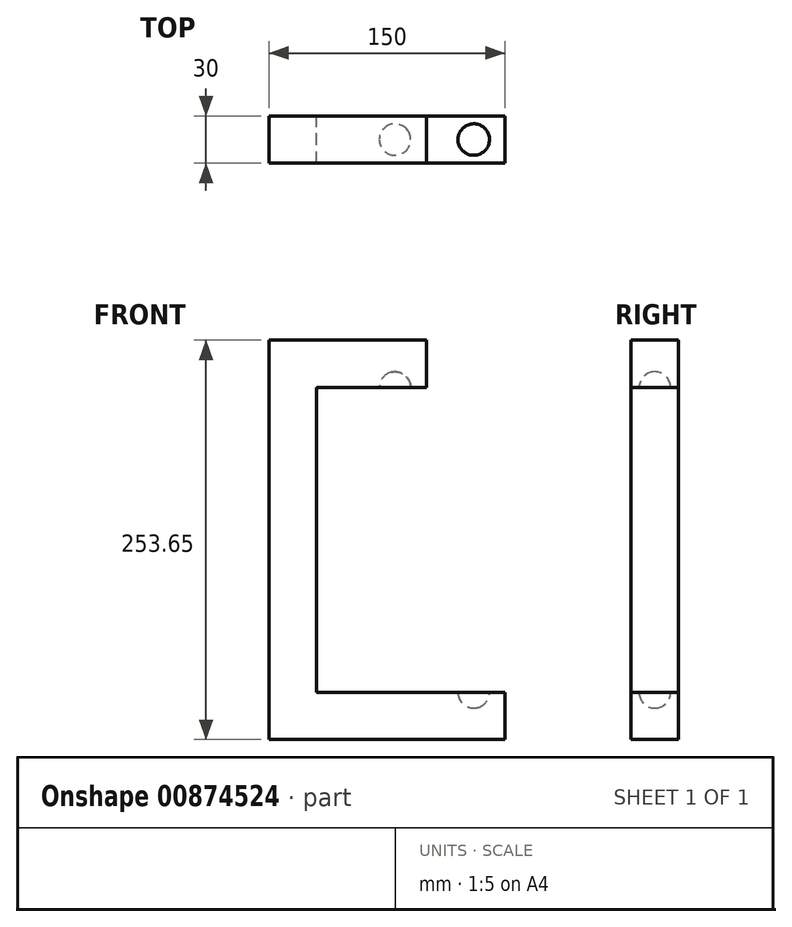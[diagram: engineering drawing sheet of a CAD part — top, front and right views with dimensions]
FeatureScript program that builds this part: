
annotation { "Feature Type Name" : "Feature", "Feature Type Description" : "" }
export const myFeature = defineFeature(function(context is Context, id is Id, definition is map)
    precondition{}
    {
        {
            var Q0;
            Q0=qCreatedBy(makeId("Front.planeOp"),FACE);
            var sketch = newSketch(context, id + "F0", { "sketchPlane" : qUnion([Q0])});
            skLineSegment(sketch, "E0", {"start": v(0, 30) * mm, "end": v(-120, 30) * mm});
            skLineSegment(sketch, "E1", {"start": v(-20, 30) * mm, "end": v(-70, 223.65) * mm, "construction": true});
            skLineSegment(sketch, "E2", {"start": v(-120, 30) * mm, "end": v(-120, 223.65) * mm});
            skLineSegment(sketch, "E3", {"start": v(-120, 223.65) * mm, "end": v(-50, 223.65) * mm});
            skLineSegment(sketch, "E4", {"start": v(-50, 223.65) * mm, "end": v(-50, 253.65) * mm});
            skLineSegment(sketch, "E5", {"start": v(-50, 253.65) * mm, "end": v(-150, 253.65) * mm});
            skLineSegment(sketch, "E6", {"start": v(-150, 253.65) * mm, "end": v(-150, 0) * mm});
            skLineSegment(sketch, "E7", {"start": v(-150, 0) * mm, "end": v(0, 0) * mm});
            skLineSegment(sketch, "E8", {"start": v(0, 0) * mm, "end": v(0, 30) * mm});
            skSolve(sketch);
        }
        {
            var Q0;
            Q0 = qSketchRegion(id + "F0", true);
            extrude(context, id + "F1", {"entities" : qUnion([Q0]), "endBound" : BoundingType.SYMMETRIC, "depth" : 30 * mm, "offsetDistance" : 25 * mm});
        }
        {
            var Q0;
            Q0=qCreatedBy(makeId("Front.planeOp"),FACE);
            var sketch = newSketch(context, id + "F2", { "sketchPlane" : qUnion([Q0])});
            skLineSegment(sketch, "E9", {"start": v(-17.5, 20.32) * mm, "end": v(-72.5, 233.33) * mm, "construction": true});
            skArc(sketch, "E10", {"start": v(-67.5, 213.97) * mm, "mid": v(-60.32, 226.15) * mm, "end": v(-72.5, 233.33) * mm});
            skArc(sketch, "E11", {"start": v(-17.5, 20.32) * mm, "mid": v(-10.32, 32.5) * mm, "end": v(-22.5, 39.68) * mm});
            skLineSegment(sketch, "E12", {"start": v(-72.5, 233.33) * mm, "end": v(-67.5, 213.97) * mm});
            skLineSegment(sketch, "E13", {"start": v(-22.5, 39.68) * mm, "end": v(-17.5, 20.32) * mm});
            skSolve(sketch);
        }
        {
            var Q0;
            Q0=makeQuery(id+"F2.imprint","IMPRINT",FACE,{"disambiguationData":[TD([[makeQuery(id+"F2.imprint","IMPRINT",EDGE,{"derivedFrom":sQuery(id+"F2.wireOp",EDGE,"E11")}),1.0]])]});
            var Q1;
            Q1=makeQuery(id+"F2.imprint","IMPRINT",FACE,{"disambiguationData":[TD([[makeQuery(id+"F2.imprint","IMPRINT",EDGE,{"derivedFrom":sQuery(id+"F2.wireOp",EDGE,"E10")}),1.0]])]});
            var Q2;
            Q2=sQuery(id+"F2.wireOp",EDGE,"E10");
            var Q3;
            Q3=sQuery(id+"F2.wireOp",EDGE,"E11");
            var Q4;
            Q4=sQuery(id+"F2.wireOp",EDGE,"E9");
            revolve(context, id + "F3", {"operationType" : NewBodyOperationType.REMOVE, "surfaceOperationType" : NewSurfaceOperationType.NEW, "entities" : qUnion([Q0, Q1]), "surfaceEntities" : qUnion([Q2, Q3]), "axis" : qUnion([Q4]), "revolveType" : RevolveType.FULL});
        }
    });
